# Revit family: Toilet_Tissue_Holder-Wall_Mounted-American_Standard-C_Series-8337.230
name_source: partatom
category: Specialty Equipment
revit_build: Autodesk Revit 2014 (Build: 20130308_1515(x64)
units: mm (PartAtom-declared; Revit-internal decimal feet)

## types (1)
- 8337.230
    Assembly Code = C1030220
    Default Elevation = 20"
    Description = C Series Toilet Paper Holder.
    Height = 2"
    Installation Type = Wall Mounted
    Length = 4 11/16"
    Manufacturer = American Standard
    Material = Metal-American Standard-002-Polished Chrome
    Model = 8337.230
    Product Documentation Link = https://www.americanstandard-us.com
    Product Page URL = https://www.americanstandard-us.com
    Revised Date = 02/08/2016
    Type Comments = Available Finishes Include Chrome Polished, Oil Rubbed Bronze & Satin Nickel.
    URL = http://www.americanstandard-us.com
    Warranty Information = 1 Year Warranty
    Width = 8 1/4"

## geometry (parser evidence)
native form markers: Sweep x3
no freeform markers — native parametric forms only
